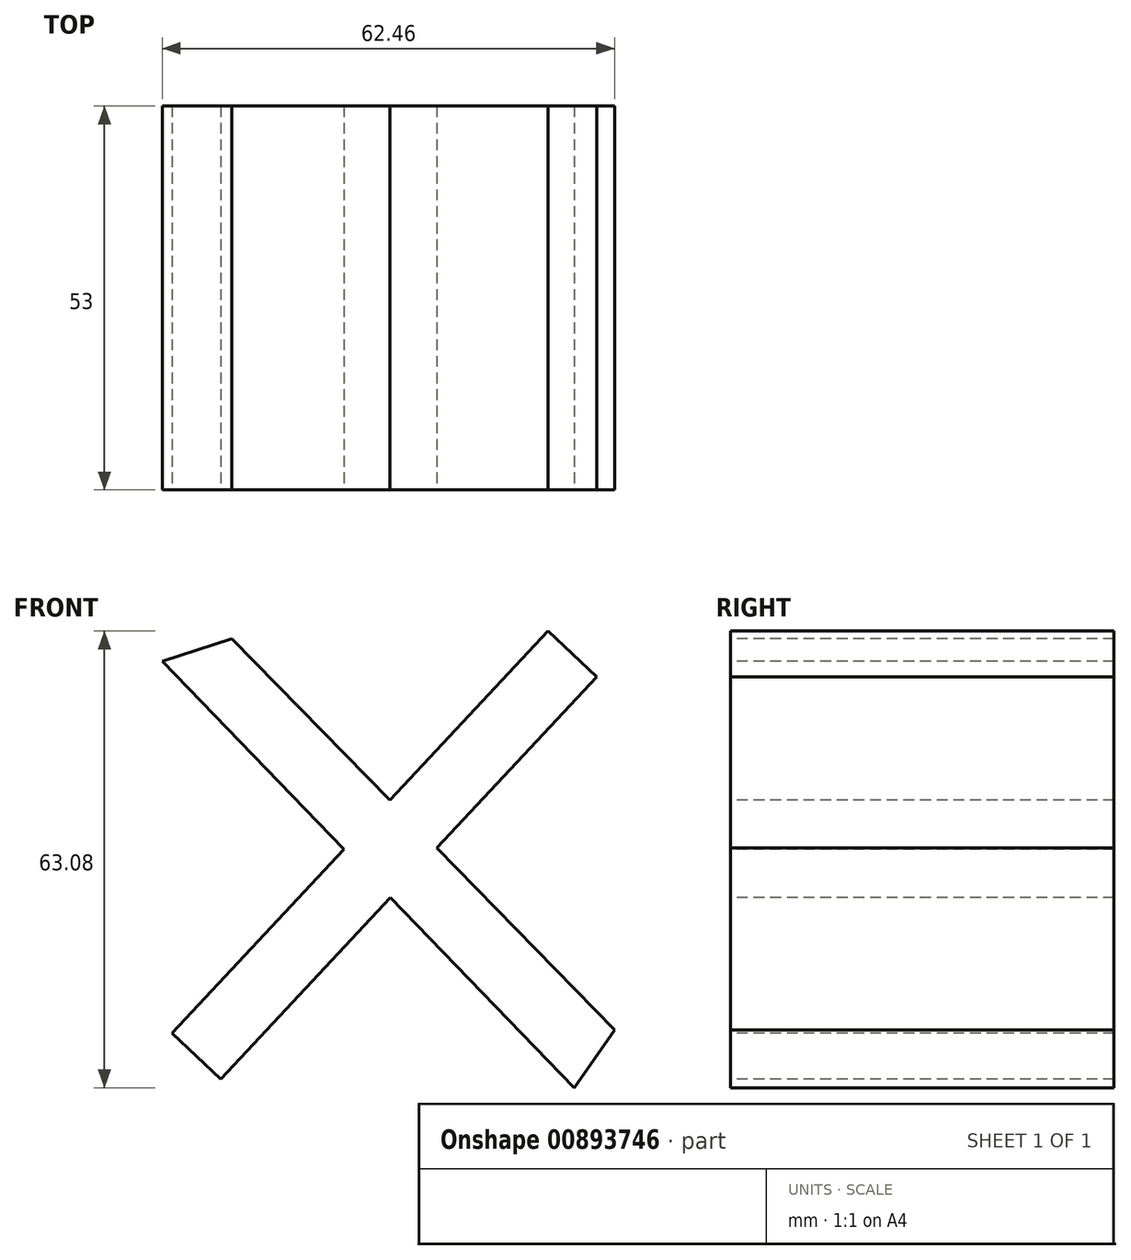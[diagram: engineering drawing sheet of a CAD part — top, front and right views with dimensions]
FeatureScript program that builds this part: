
annotation { "Feature Type Name" : "Feature", "Feature Type Description" : "" }
export const myFeature = defineFeature(function(context is Context, id is Id, definition is map)
    precondition{}
    {
        {
            var Q0;
            Q0=qCreatedBy(makeId("Front.planeOp"),FACE);
            var sketch = newSketch(context, id + "F0", { "sketchPlane" : qUnion([Q0])});
            skLineSegment(sketch, "E0.bottom", {"start": v(33.5, -33.5) * mm, "end": v(-33.5, -33.5) * mm});
            skLineSegment(sketch, "E0.top", {"start": v(33.5, 33.5) * mm, "end": v(-33.5, 33.5) * mm});
            skLineSegment(sketch, "E0.left", {"start": v(33.5, -33.5) * mm, "end": v(33.5, 33.5) * mm});
            skLineSegment(sketch, "E0.right", {"start": v(-33.5, -33.5) * mm, "end": v(-33.5, 33.5) * mm});
            skPoint(sketch, "E0.middle", {"position": v(0, 0) * mm});
            skLineSegment(sketch, "E1", {"start": v(-33.5, -29.05) * mm, "end": v(25, 33.5) * mm});
            skLineSegment(sketch, "E2", {"start": v(-25, -33.5) * mm, "end": v(33.5, 29.05) * mm});
            skLineSegment(sketch, "E3", {"start": v(-33.5, 29.53) * mm, "end": v(27.4, -33.5) * mm});
            skLineSegment(sketch, "E4", {"start": v(-24.76, 33.5) * mm, "end": v(33.5, -26.1) * mm});
            skLineSegment(sketch, "E5", {"start": v(-30.74, 26.68) * mm, "end": v(-21.14, 29.8) * mm});
            skLineSegment(sketch, "E6", {"start": v(22.51, 30.85) * mm, "end": v(29.27, 24.53) * mm});
            skLineSegment(sketch, "E7", {"start": v(31.72, -24.28) * mm, "end": v(26.17, -32.23) * mm});
            skLineSegment(sketch, "E8", {"start": v(-29.44, -24.7) * mm, "end": v(-22.68, -31.02) * mm});
            skSolve(sketch);
        }
        {
            var Q0;
            {var subQ5=sQuery(id+"F0.wireOp",EDGE,"E5");Q0=makeQuery(id+"F0.imprint","IMPRINT",FACE,{"disambiguationData":[TD([[makeQuery(id+"F0.imprint","IMPRINT",EDGE,{"derivedFrom":subQ5}),-1.0]])]});}
            var Q1;
            {var subQ0=sQuery(id+"F0.wireOp",EDGE,"E6");Q1=makeQuery(id+"F0.imprint","IMPRINT",FACE,{"disambiguationData":[TD([[makeQuery(id+"F0.imprint","IMPRINT",EDGE,{"derivedFrom":subQ0}),-1.0]])]});}
            var Q2;
            {var subQ5=sQuery(id+"F0.wireOp",EDGE,"E7");Q2=makeQuery(id+"F0.imprint","IMPRINT",FACE,{"disambiguationData":[TD([[makeQuery(id+"F0.imprint","IMPRINT",EDGE,{"derivedFrom":subQ5}),-1.0]])]});}
            var Q3;
            {var subQ0=sQuery(id+"F0.wireOp",EDGE,"E3");var subQ1=sQuery(id+"F0.wireOp",EDGE,"E1");var subQ2=makeQuery(id+"F0.imprint","INTERSECT",VERTEX,{"derivedFrom":[subQ1,subQ0]});Q3=makeQuery(id+"F0.imprint","IMPRINT",FACE,{"disambiguationData":[TD([[makeQuery(id+"F0.imprint","IMPRINT",EDGE,{"disambiguationData":[TD([[subQ2,-1.0]])],"derivedFrom":subQ1}),-1.0]])]});}
            var Q4;
            {var subQ0=sQuery(id+"F0.wireOp",EDGE,"E1");var subQ1=makeQuery(id+"F0.imprint","IMPRINT",VERTEX,{"derivedFrom":subQ0});Q4=makeQuery(id+"F0.imprint","IMPRINT",FACE,{"disambiguationData":[TD([[makeQuery(id+"F0.imprint","IMPRINT",EDGE,{"disambiguationData":[TD([[subQ1,1.0]])],"derivedFrom":subQ0}),-1.0]])]});}
            var Q5;
            {var subQ0=sQuery(id+"F0.wireOp",EDGE,"zUPrBjbI-q0Hu-6jQr-QFBf-zmR45OrmYaUR");Q5=makeQuery(id+"F0.imprint","IMPRINT",FACE,{"disambiguationData":[TD([[makeQuery(id+"F0.imprint","IMPRINT",EDGE,{"derivedFrom":subQ0}),1.0]])]});}
            var Q6;
            {var subQ0=sQuery(id+"F0.wireOp",EDGE,"yp1y907L-ZFzm-RHuy-K6kK-Zlu4iT2xUe7O");Q6=makeQuery(id+"F0.imprint","IMPRINT",FACE,{"disambiguationData":[TD([[makeQuery(id+"F0.imprint","IMPRINT",EDGE,{"derivedFrom":subQ0}),1.0]])]});}
            var Q7;
            {var subQ0=sQuery(id+"F0.wireOp",EDGE,"E8");Q7=makeQuery(id+"F0.imprint","IMPRINT",FACE,{"disambiguationData":[TD([[makeQuery(id+"F0.imprint","IMPRINT",EDGE,{"derivedFrom":subQ0}),1.0]])]});}
            extrude(context, id + "F1", {"entities" : qUnion([Q0, Q1, Q2, Q3, Q4, Q5, Q6, Q7]), "oppositeDirection" : true, "depth" : 53 * mm, "offsetDistance" : 25 * mm});
        }
    });
